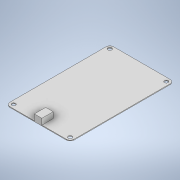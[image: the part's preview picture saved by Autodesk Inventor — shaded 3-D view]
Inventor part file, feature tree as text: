
AUTODESK INVENTOR PART (.ipt)
format: ipt  version: 2022 (Build 260153000, 153)  size: 254,464 bytes
history: native  units: mm
features: extrude x4, sketch x4, fillet x1, pattern_linear x1
ambient origin geometry x8: Origin, YZ Plane, XZ Plane, XY Plane, X Axis, Y Axis, Z Axis, Center Point
bodies: Solid1 (feature_tree)
feature tree (10):
  extrude  "Extrusion1"  Depth=275.0mm
  fillet  "Fillet1"  Radius=2.0mm
  extrude  "Extrusion2"  Depth=85.0mm
  extrude  "Extrusion3"  Depth=20.0mm
  pattern_linear  "Rectangular Pattern1"  Spacing1=15.0mm  [1 undecoded]
  extrude  "Extrusion4"  Depth=150.0mm
  sketch  "Sketch1"  dims[d0=170.0mm d1=275.0mm d2=2.0mm d3=0.0mm]
  sketch  "Sketch2"  dims[d4=10.0mm d5=85.0mm]
  sketch  "Sketch3"  dims[d6=30.0mm d7=20.0mm]
  sketch  "Sketch4"  dims[d8=15.75mm d9=0.0mm d10=15.0mm d11=150.0mm d12=0.3mm d13=0.0mm d14=120.0mm d16=20.0mm d17=25.0mm d18=10.0mm d19=20.0mm d21=255.0mm d22=20.0mm d24=150.0mm d27=0.0mm d28=0.0mm]
note: 1 required parameter value undecoded (feature->parameter linkage not recoverable at this tier; creation-order binding heuristic only, values carry confidence <= 0.55)
